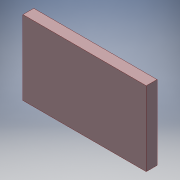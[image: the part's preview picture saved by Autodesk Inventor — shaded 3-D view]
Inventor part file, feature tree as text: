
AUTODESK INVENTOR PART (.ipt)
format: ipt  version: 2019.3 (Build 233278000, 278)  size: 96,768 bytes
history: native  units: mm
features: extrude x1, sketch x1
ambient origin geometry x8: Origin, YZ Plane, XZ Plane, XY Plane, X Axis, Y Axis, Z Axis, Center Point
bodies: Solid1 (feature_tree)
feature tree (2):
  extrude  "Extrusion1"  Depth=110.5mm
  sketch  "Sketch1"  dims[d0=183.0mm d1=110.5mm d2=16.0mm d3=0.0mm]
